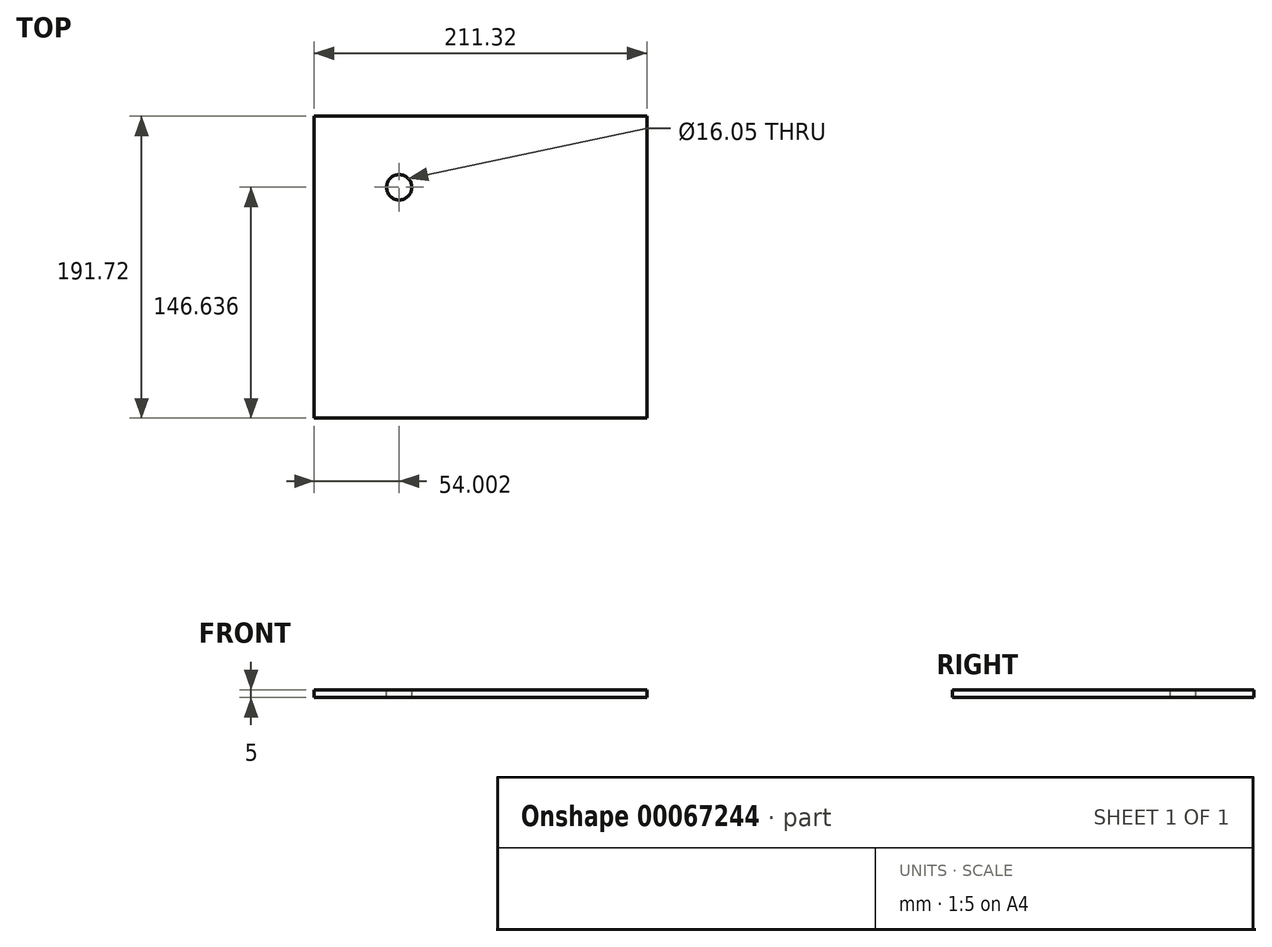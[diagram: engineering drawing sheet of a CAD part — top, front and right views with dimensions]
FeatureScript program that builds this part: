
annotation { "Feature Type Name" : "Feature", "Feature Type Description" : "" }
export const myFeature = defineFeature(function(context is Context, id is Id, definition is map)
    precondition{}
    {
        {
            var Q0;
            Q0=qCreatedBy(makeId("Top.planeOp"),FACE);
            var sketch = newSketch(context, id + "F0", { "sketchPlane" : qUnion([Q0])});
            skLineSegment(sketch, "E0.rect.bottom", {"start": v(-105.66, 95.86) * mm, "end": v(105.66, 95.86) * mm});
            skLineSegment(sketch, "E0.rect.top", {"start": v(-105.66, -95.86) * mm, "end": v(105.66, -95.86) * mm});
            skLineSegment(sketch, "E0.rect.left", {"start": v(-105.66, 95.86) * mm, "end": v(-105.66, -95.86) * mm});
            skLineSegment(sketch, "E0.rect.right", {"start": v(105.66, 95.86) * mm, "end": v(105.66, -95.86) * mm});
            skPoint(sketch, "E0.rect.middle", {"position": v(0, 0) * mm});
            skSolve(sketch);
        }
        {
            var Q0;
            Q0 = qSketchRegion(id + "F0", true);
            extrude(context, id + "F1", {"entities" : qUnion([Q0]), "endBound" : BoundingType.SYMMETRIC, "depth" : 5 * mm});
        }
        {
            var Q0;
            Q0=makeQuery(id+"F1.opExtrude","CAP_FACE",FACE,{"disambiguationData":[OSD([sQuery(id+"F0.wireOp",EDGE,"E0.rect.bottom"),sQuery(id+"F0.wireOp",EDGE,"E0.rect.top"),sQuery(id+"F0.wireOp",EDGE,"E0.rect.left"),sQuery(id+"F0.wireOp",EDGE,"E0.rect.right")])],"isStart":false});
            var sketch = newSketch(context, id + "F2", { "sketchPlane" : qUnion([Q0])});
            skCircle(sketch, "E1", {"center": v(-51.66, 50.78) * mm, "radius": 8.03 * mm});
            skSolve(sketch);
        }
        {
            var Q0;
            Q0 = qSketchRegion(id + "F2", true);
            extrude(context, id + "F3", {"entities" : qUnion([Q0]), "operationType" : NewBodyOperationType.REMOVE, "endBound" : BoundingType.THROUGH_ALL, "oppositeDirection" : true, "depth" : 25 * mm});
        }
    });
